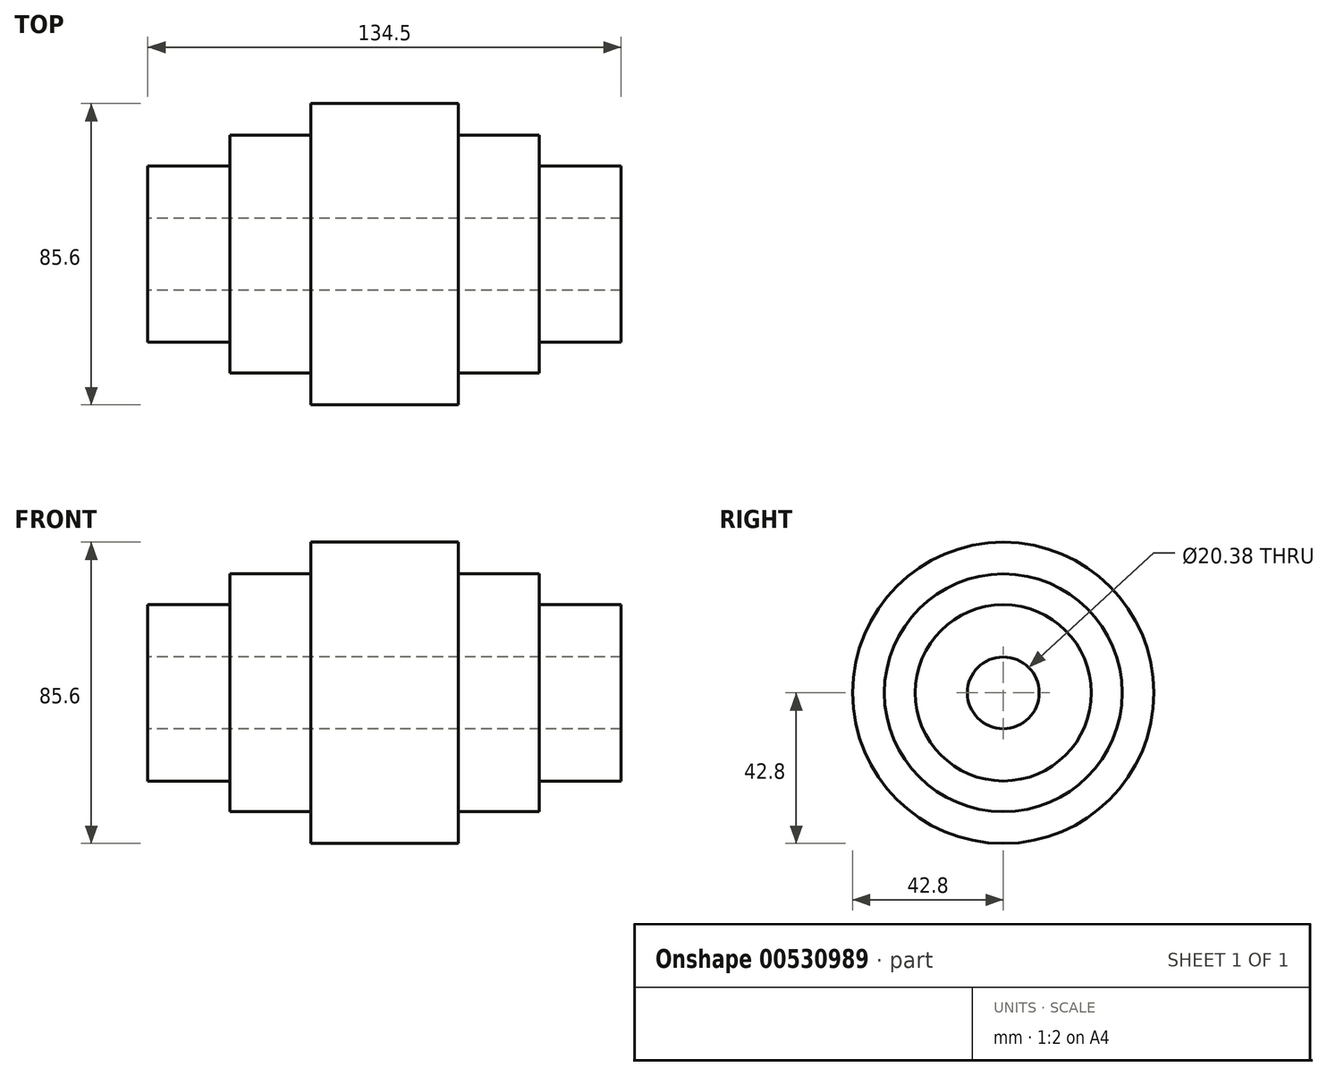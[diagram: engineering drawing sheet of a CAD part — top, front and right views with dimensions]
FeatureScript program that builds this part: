
annotation { "Feature Type Name" : "Feature", "Feature Type Description" : "" }
export const myFeature = defineFeature(function(context is Context, id is Id, definition is map)
    precondition{}
    {
        {
            var Q0;
            Q0=qCreatedBy(makeId("Front.planeOp"),FACE);
            var sketch = newSketch(context, id + "F0", { "sketchPlane" : qUnion([Q0])});
            skLineSegment(sketch, "E0.bottom", {"start": v(0, 42.8) * mm, "end": v(20.96, 42.8) * mm});
            skLineSegment(sketch, "E0.top", {"start": v(0, 10.19) * mm, "end": v(20.96, 10.19) * mm});
            skLineSegment(sketch, "E0.left", {"start": v(0, 42.8) * mm, "end": v(0, 10.19) * mm});
            skLineSegment(sketch, "E0.right", {"start": v(20.96, 42.8) * mm, "end": v(20.96, 10.19) * mm});
            skLineSegment(sketch, "E1.bottom", {"start": v(20.96, 33.77) * mm, "end": v(43.96, 33.77) * mm});
            skLineSegment(sketch, "E1.top", {"start": v(20.96, 10.19) * mm, "end": v(43.96, 10.19) * mm});
            skLineSegment(sketch, "E1.left", {"start": v(20.96, 33.77) * mm, "end": v(20.96, 10.19) * mm});
            skLineSegment(sketch, "E1.right", {"start": v(43.96, 33.77) * mm, "end": v(43.96, 10.19) * mm});
            skLineSegment(sketch, "E2.bottom", {"start": v(43.96, 25.04) * mm, "end": v(67.25, 25.04) * mm});
            skLineSegment(sketch, "E2.top", {"start": v(43.96, 10.19) * mm, "end": v(67.25, 10.19) * mm});
            skLineSegment(sketch, "E2.left", {"start": v(43.96, 25.04) * mm, "end": v(43.96, 10.19) * mm});
            skLineSegment(sketch, "E2.right", {"start": v(67.25, 25.04) * mm, "end": v(67.25, 10.19) * mm});
            skLineSegment(sketch, "E3.MirrorCS", {"start": v(0, 42.8) * mm, "end": v(-20.96, 42.8) * mm});
            skLineSegment(sketch, "E4.MirrorCS", {"start": v(-20.96, 42.8) * mm, "end": v(-20.96, 10.19) * mm});
            skLineSegment(sketch, "E5.MirrorCS", {"start": v(-20.96, 33.77) * mm, "end": v(-43.96, 33.77) * mm});
            skLineSegment(sketch, "E6.MirrorCS", {"start": v(-43.96, 33.77) * mm, "end": v(-43.96, 10.19) * mm});
            skLineSegment(sketch, "E7.MirrorCS", {"start": v(-43.96, 25.04) * mm, "end": v(-67.25, 25.04) * mm});
            skLineSegment(sketch, "E8.MirrorCS", {"start": v(-67.25, 25.04) * mm, "end": v(-67.25, 10.19) * mm});
            skLineSegment(sketch, "E9.MirrorCS", {"start": v(-43.96, 10.19) * mm, "end": v(-67.25, 10.19) * mm});
            skLineSegment(sketch, "E10.MirrorCS", {"start": v(-20.96, 10.19) * mm, "end": v(-43.96, 10.19) * mm});
            skLineSegment(sketch, "E11.MirrorCS", {"start": v(0, 10.19) * mm, "end": v(-20.96, 10.19) * mm});
            skLineSegment(sketch, "E12", {"start": v(-56.48, 0) * mm, "end": v(39.01, 0) * mm});
            skSolve(sketch);
        }
        {
            var Q0;
            Q0=makeQuery(id+"F0.imprint","IMPRINT",FACE,{"disambiguationData":[TD([[makeQuery(id+"F0.imprint","IMPRINT",EDGE,{"derivedFrom":sQuery(id+"F0.wireOp",EDGE,"E0.bottom")}),-1.0]])]});
            var Q1;
            {var subQ3=sQuery(id+"F0.wireOp",EDGE,"E5.MirrorCS");Q1=makeQuery(id+"F0.imprint","IMPRINT",FACE,{"disambiguationData":[TD([[makeQuery(id+"F0.imprint","IMPRINT",EDGE,{"derivedFrom":subQ3}),1.0]])]});}
            var Q2;
            {var subQ2=sQuery(id+"F0.wireOp",EDGE,"E7.MirrorCS");Q2=makeQuery(id+"F0.imprint","IMPRINT",FACE,{"disambiguationData":[TD([[makeQuery(id+"F0.imprint","IMPRINT",EDGE,{"derivedFrom":subQ2}),1.0]])]});}
            var Q3;
            Q3=makeQuery(id+"F0.imprint","IMPRINT",FACE,{"disambiguationData":[TD([[makeQuery(id+"F0.imprint","IMPRINT",EDGE,{"derivedFrom":sQuery(id+"F0.wireOp",EDGE,"E0.left")}),-1.0]])]});
            var Q4;
            Q4=makeQuery(id+"F0.imprint","IMPRINT",FACE,{"disambiguationData":[TD([[makeQuery(id+"F0.imprint","IMPRINT",EDGE,{"derivedFrom":sQuery(id+"F0.wireOp",EDGE,"E1.bottom")}),-1.0]])]});
            var Q5;
            Q5=makeQuery(id+"F0.imprint","IMPRINT",FACE,{"disambiguationData":[TD([[makeQuery(id+"F0.imprint","IMPRINT",EDGE,{"derivedFrom":sQuery(id+"F0.wireOp",EDGE,"E2.bottom")}),-1.0]])]});
            var Q6;
            Q6=sQuery(id+"F0.wireOp",EDGE,"E12");
            revolve(context, id + "F1", {"entities" : qUnion([Q0, Q1, Q2, Q3, Q4, Q5]), "axis" : qUnion([Q6]), "revolveType" : RevolveType.FULL});
        }
    });
